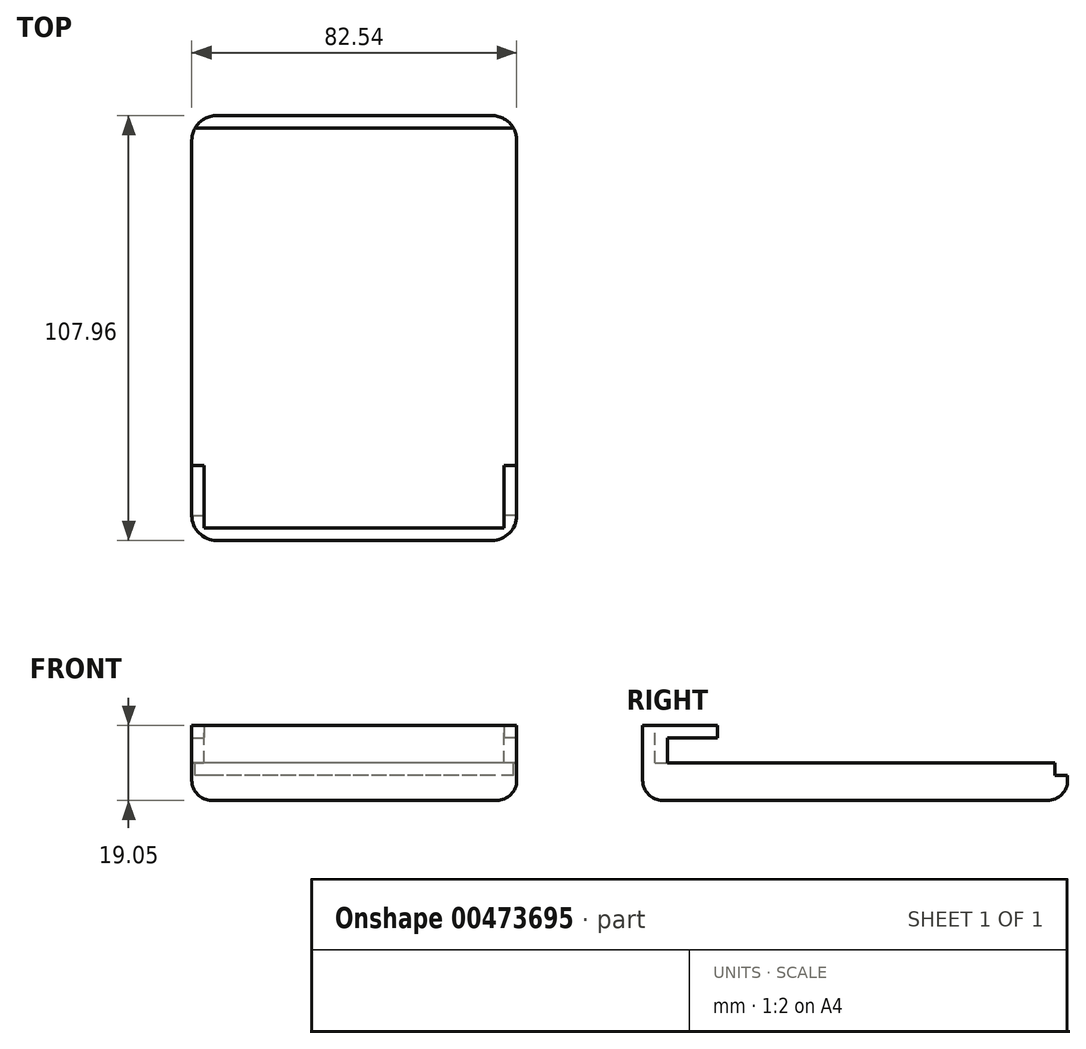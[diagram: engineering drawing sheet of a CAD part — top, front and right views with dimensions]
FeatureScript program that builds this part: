
annotation { "Feature Type Name" : "Feature", "Feature Type Description" : "" }
export const myFeature = defineFeature(function(context is Context, id is Id, definition is map)
    precondition{}
    {
        {
            var Q0;
            Q0=qCreatedBy(makeId("Top.planeOp"),FACE);
            var sketch = newSketch(context, id + "F0", { "sketchPlane" : qUnion([Q0])});
            skPoint(sketch, "E0.middle", {"position": v(0, 0) * mm});
            skLineSegment(sketch, "E1.0", {"start": v(34.93, 53.98) * mm, "end": v(-34.93, 53.98) * mm});
            skLineSegment(sketch, "E1.1", {"start": v(41.28, 47.63) * mm, "end": v(41.28, -47.63) * mm});
            skLineSegment(sketch, "E1.2", {"start": v(34.93, -53.98) * mm, "end": v(-34.93, -53.98) * mm});
            skLineSegment(sketch, "E1.3", {"start": v(-41.28, 47.63) * mm, "end": v(-41.28, -47.63) * mm});
            skArc(sketch, "E2", {"start": v(-34.93, 53.98) * mm, "mid": v(-39.42, 52.12) * mm, "end": v(-41.28, 47.63) * mm});
            skArc(sketch, "E3", {"start": v(41.28, 47.63) * mm, "mid": v(39.42, 52.12) * mm, "end": v(34.93, 53.98) * mm});
            skArc(sketch, "E4", {"start": v(34.93, -53.98) * mm, "mid": v(39.42, -52.12) * mm, "end": v(41.28, -47.63) * mm});
            skArc(sketch, "E5", {"start": v(-41.28, -47.63) * mm, "mid": v(-39.42, -52.12) * mm, "end": v(-34.93, -53.98) * mm});
            skSolve(sketch);
        }
        {
            var Q0;
            Q0=makeQuery(id+"F0.imprint","IMPRINT",FACE,{"disambiguationData":[TD([[makeQuery(id+"F0.imprint","IMPRINT",EDGE,{"derivedFrom":sQuery(id+"F0.wireOp",EDGE,"E1.0")}),1.0]])]});
            extrude(context, id + "F1", {"entities" : qUnion([Q0]), "depth" : 19.05 * mm});
        }
        {
            var Q0;
            Q0=makeQuery(id+"F1.opExtrude","CAP_EDGE",EDGE,{"disambiguationData":[OSD([sQuery(id+"F0.wireOp",EDGE,"E1.2")])],"isStart":true});
            fillet(context, id + "F2", {"entities" : qUnion([Q0]), "radius" : 5.08 * mm, "tangentPropagation" : true, "allowEdgeOverflow" : false});
        }
        {
            var Q0;
            Q0=makeQuery(id+"F1.opExtrude","CAP_FACE",FACE,{"disambiguationData":[OSD([sQuery(id+"F0.wireOp",EDGE,"E1.0"),sQuery(id+"F0.wireOp",EDGE,"E1.1"),sQuery(id+"F0.wireOp",EDGE,"E1.2"),sQuery(id+"F0.wireOp",EDGE,"E1.3"),sQuery(id+"F0.wireOp",EDGE,"E2"),sQuery(id+"F0.wireOp",EDGE,"E3"),sQuery(id+"F0.wireOp",EDGE,"E4"),sQuery(id+"F0.wireOp",EDGE,"E5")])],"isStart":false});
            var sketch = newSketch(context, id + "F3", { "sketchPlane" : qUnion([Q0])});
            skLineSegment(sketch, "E6.0", {"start": v(38.1, 50.8) * mm, "end": v(-38.1, 50.8) * mm});
            skLineSegment(sketch, "E6.1", {"start": v(38.1, 50.8) * mm, "end": v(38.1, -50.8) * mm});
            skLineSegment(sketch, "E6.2", {"start": v(38.1, -50.8) * mm, "end": v(-38.1, -50.8) * mm});
            skLineSegment(sketch, "E6.3", {"start": v(-38.1, 50.8) * mm, "end": v(-38.1, -50.8) * mm});
            skLineSegment(sketch, "E7.0", {"start": v(41.28, 53.98) * mm, "end": v(-34.93, 53.98) * mm});
            skLineSegment(sketch, "E7.1", {"start": v(41.28, -47.63) * mm, "end": v(41.28, 53.98) * mm});
            skSolve(sketch);
        }
        {
            var Q0;
            Q0=makeQuery(id+"F3.imprint","IMPRINT",FACE,{"disambiguationData":[TD([[makeQuery(id+"F3.imprint","IMPRINT",EDGE,{"derivedFrom":sQuery(id+"F3.wireOp",EDGE,"E6.0")}),1.0]])]});
            extrude(context, id + "F4", {"entities" : qUnion([Q0]), "operationType" : NewBodyOperationType.REMOVE, "oppositeDirection" : true, "depth" : 9.52 * mm});
        }
        {
            var Q0;
            Q0=makeQuery(id+"F1.opExtrude","CAP_FACE",FACE,{"disambiguationData":[OSD([sQuery(id+"F0.wireOp",EDGE,"E1.0"),sQuery(id+"F0.wireOp",EDGE,"E1.1"),sQuery(id+"F0.wireOp",EDGE,"E1.2"),sQuery(id+"F0.wireOp",EDGE,"E1.3"),sQuery(id+"F0.wireOp",EDGE,"E2"),sQuery(id+"F0.wireOp",EDGE,"E3"),sQuery(id+"F0.wireOp",EDGE,"E4"),sQuery(id+"F0.wireOp",EDGE,"E5")])],"isStart":false});
            var sketch = newSketch(context, id + "F5", { "sketchPlane" : qUnion([Q0])});
            skLineSegment(sketch, "E8", {"start": v(-40.42, 50.8) * mm, "end": v(40.42, 50.8) * mm});
            skSolve(sketch);
        }
        {
            var Q0;
            {var subQ0=makeQuery(id+"F1.opExtrude","CAP_EDGE",EDGE,{"disambiguationData":[OSD([sQuery(id+"F0.wireOp",EDGE,"E1.0")])],"isStart":false});Q0=makeQuery(id+"F5.imprint","IMPRINT",FACE,{"disambiguationData":[TD([[makeQuery(id+"F5.imprint","IMPRINT",EDGE,{"derivedFrom":subQ0}),1.0]])]});}
            extrude(context, id + "F6", {"entities" : qUnion([Q0]), "operationType" : NewBodyOperationType.REMOVE, "oppositeDirection" : true, "depth" : 12.7 * mm});
        }
        {
            var Q0;
            Q0=makeQuery(id+"F4.boolean.opBoolean","COPY",FACE,{"derivedFrom":makeQuery(id+"F4.opExtrude","SWEPT_FACE",FACE,{"disambiguationData":[OSD([sQuery(id+"F3.wireOp",EDGE,"E6.1")])]})});
            var sketch = newSketch(context, id + "F7", { "sketchPlane" : qUnion([Q0])});
            skLineSegment(sketch, "E9.bottom", {"start": v(50.8, 19.05) * mm, "end": v(34.93, 19.05) * mm});
            skLineSegment(sketch, "E9.top", {"start": v(50.8, 15.88) * mm, "end": v(34.93, 15.88) * mm});
            skLineSegment(sketch, "E9.left", {"start": v(50.8, 19.05) * mm, "end": v(50.8, 15.88) * mm});
            skLineSegment(sketch, "E9.right", {"start": v(34.93, 19.05) * mm, "end": v(34.93, 15.88) * mm});
            skSolve(sketch);
        }
        {
            var Q0;
            {var subQ9=sQuery(id+"F7.wireOp",EDGE,"E9.top");Q0=makeQuery(id+"F7.imprint","IMPRINT",FACE,{"disambiguationData":[TD([[makeQuery(id+"F7.imprint","IMPRINT",EDGE,{"derivedFrom":subQ9}),1.0]])]});}
            extrude(context, id + "F8", {"entities" : qUnion([Q0]), "operationType" : NewBodyOperationType.REMOVE, "oppositeDirection" : true, "depth" : 25.4 * mm});
        }
        {
            var Q0;
            Q0=makeQuery(id+"F4.boolean.opBoolean","COPY",FACE,{"derivedFrom":makeQuery(id+"F4.opExtrude","SWEPT_FACE",FACE,{"disambiguationData":[OSD([sQuery(id+"F3.wireOp",EDGE,"E6.3")])]})});
            var sketch = newSketch(context, id + "F9", { "sketchPlane" : qUnion([Q0])});
            skLineSegment(sketch, "E10.bottom", {"start": v(-50.8, 19.05) * mm, "end": v(-34.93, 19.05) * mm});
            skLineSegment(sketch, "E10.top", {"start": v(-50.8, 15.88) * mm, "end": v(-34.93, 15.88) * mm});
            skLineSegment(sketch, "E10.left", {"start": v(-50.8, 19.05) * mm, "end": v(-50.8, 15.88) * mm});
            skLineSegment(sketch, "E10.right", {"start": v(-34.93, 19.05) * mm, "end": v(-34.93, 15.88) * mm});
            skSolve(sketch);
        }
        {
            var Q0;
            {var subQ9=sQuery(id+"F9.wireOp",EDGE,"E10.top");Q0=makeQuery(id+"F9.imprint","IMPRINT",FACE,{"disambiguationData":[TD([[makeQuery(id+"F9.imprint","IMPRINT",EDGE,{"derivedFrom":subQ9}),-1.0]])]});}
            extrude(context, id + "F10", {"entities" : qUnion([Q0]), "operationType" : NewBodyOperationType.REMOVE, "oppositeDirection" : true, "depth" : 3.17 * mm});
        }
        {
            var Q0;
            Q0=makeQuery(id+"F8.boolean.opBoolean","COPY",FACE,{"derivedFrom":makeQuery(id+"F8.opExtrude","SWEPT_FACE",FACE,{"disambiguationData":[OSD([sQuery(id+"F7.wireOp",EDGE,"E9.top")])]})});
            var sketch = newSketch(context, id + "F11", { "sketchPlane" : qUnion([Q0])});
            skLineSegment(sketch, "E11", {"start": v(41.28, 47.63) * mm, "end": v(38.1, 47.63) * mm});
            skSolve(sketch);
        }
        {
            var Q0;
            {var subQ0=sQuery(id+"F11.wireOp",EDGE,"E11");Q0=makeQuery(id+"F11.imprint","IMPRINT",FACE,{"disambiguationData":[TD([[makeQuery(id+"F11.imprint","IMPRINT",EDGE,{"derivedFrom":subQ0}),-1.0]])]});}
            extrude(context, id + "F12", {"entities" : qUnion([Q0]), "operationType" : NewBodyOperationType.ADD, "depth" : 6.35 * mm});
        }
        {
            var Q0;
            Q0=makeQuery(id+"F10.boolean.opBoolean","COPY",FACE,{"derivedFrom":makeQuery(id+"F10.opExtrude","SWEPT_FACE",FACE,{"disambiguationData":[OSD([sQuery(id+"F9.wireOp",EDGE,"E10.top")])]})});
            var sketch = newSketch(context, id + "F13", { "sketchPlane" : qUnion([Q0])});
            skLineSegment(sketch, "E12", {"start": v(-41.28, 47.63) * mm, "end": v(-38.1, 47.63) * mm});
            skSolve(sketch);
        }
        {
            var Q0;
            {var subQ0=sQuery(id+"F13.wireOp",EDGE,"E12");Q0=makeQuery(id+"F13.imprint","IMPRINT",FACE,{"disambiguationData":[TD([[makeQuery(id+"F13.imprint","IMPRINT",EDGE,{"derivedFrom":subQ0}),1.0]])]});}
            extrude(context, id + "F14", {"entities" : qUnion([Q0]), "operationType" : NewBodyOperationType.ADD, "depth" : 6.35 * mm});
        }
    });
